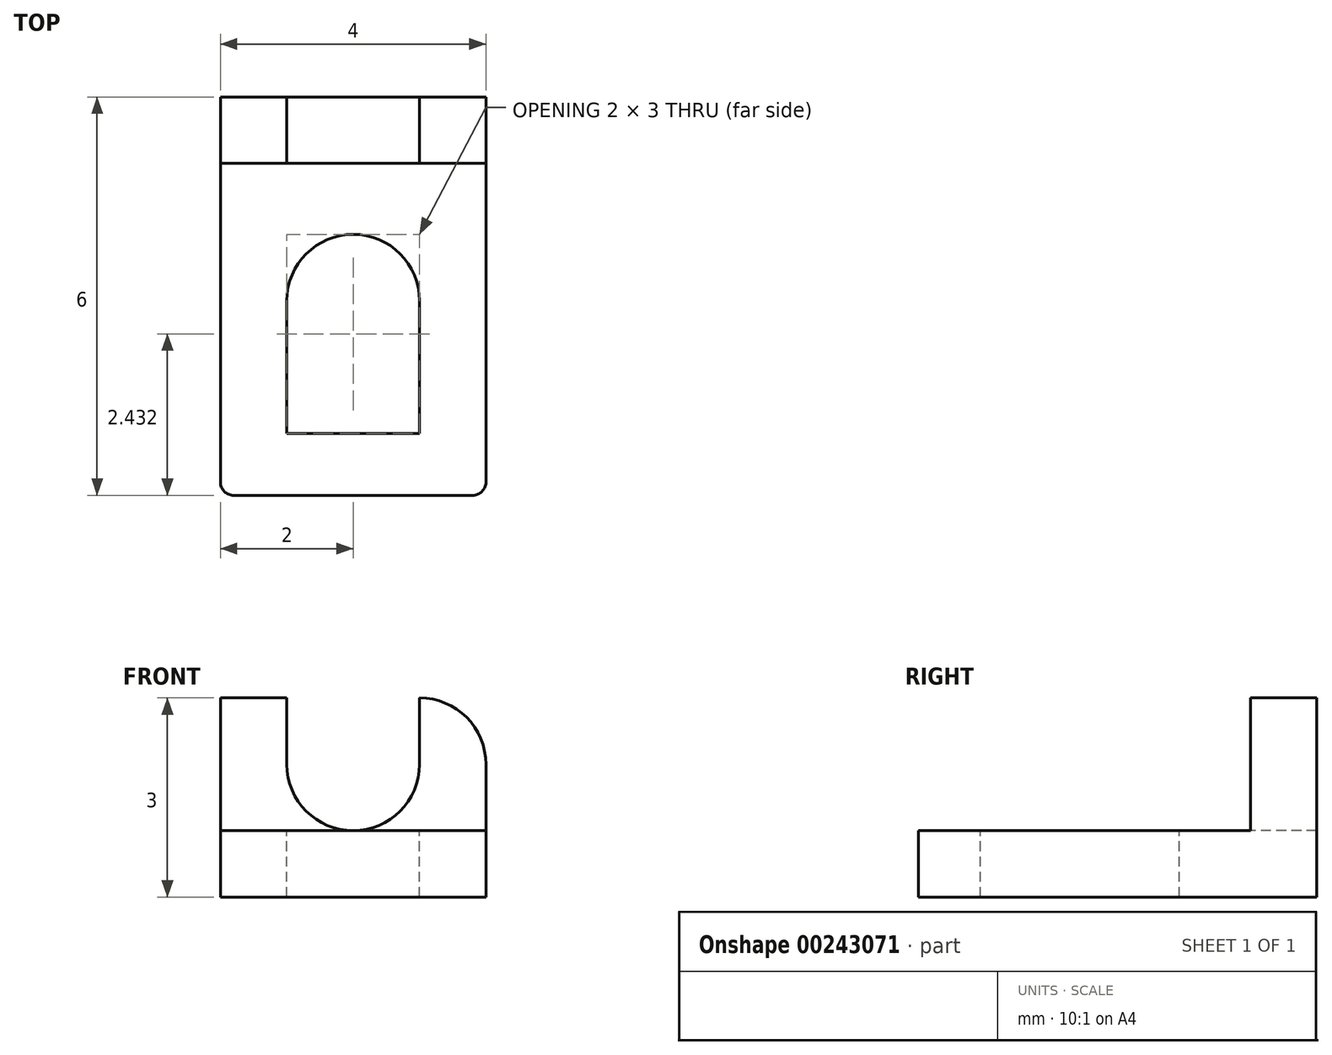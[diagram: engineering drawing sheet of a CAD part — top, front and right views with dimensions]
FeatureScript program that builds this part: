
annotation { "Feature Type Name" : "Feature", "Feature Type Description" : "" }
export const myFeature = defineFeature(function(context is Context, id is Id, definition is map)
    precondition{}
    {
        {
            var Q0;
            Q0=qCreatedBy(makeId("Top.planeOp"),FACE);
            var sketch = newSketch(context, id + "F0", { "sketchPlane" : qUnion([Q0])});
            skLineSegment(sketch, "E0.bottom", {"start": v(0, 0) * mm, "end": v(4, 0) * mm});
            skLineSegment(sketch, "E0.top", {"start": v(0, 5) * mm, "end": v(4, 5) * mm});
            skLineSegment(sketch, "E0.left", {"start": v(0, 0) * mm, "end": v(0, 5) * mm});
            skLineSegment(sketch, "E0.right", {"start": v(4, 0) * mm, "end": v(4, 5) * mm});
            skSolve(sketch);
        }
        {
            var Q0;
            Q0 = qSketchRegion(id + "F0", true);
            extrude(context, id + "F1", {"entities" : qUnion([Q0]), "depth" : 1 * mm});
        }
        {
            var Q0;
            Q0=makeQuery(id+"F1.opExtrude","SWEPT_EDGE",EDGE,{"disambiguationData":[OSD([sQuery(id+"F0.wireOp",EDGE,"E0.bottom"),sQuery(id+"F0.wireOp",EDGE,"E0.right")])]});
            fillet(context, id + "F2", {"entities" : qUnion([Q0]), "radius" : 0.2 * mm, "tangentPropagation" : true, "allowEdgeOverflow" : false});
        }
        {
            var Q0;
            Q0=makeQuery(id+"F1.opExtrude","SWEPT_EDGE",EDGE,{"disambiguationData":[OSD([sQuery(id+"F0.wireOp",EDGE,"E0.bottom"),sQuery(id+"F0.wireOp",EDGE,"E0.left")])]});
            fillet(context, id + "F3", {"entities" : qUnion([Q0]), "radius" : 0.2 * mm, "tangentPropagation" : true, "allowEdgeOverflow" : false});
        }
        {
            var Q0;
            Q0=makeQuery(id+"F1.opExtrude","CAP_FACE",FACE,{"disambiguationData":[OSD([sQuery(id+"F0.wireOp",EDGE,"E0.bottom"),sQuery(id+"F0.wireOp",EDGE,"E0.top"),sQuery(id+"F0.wireOp",EDGE,"E0.left"),sQuery(id+"F0.wireOp",EDGE,"E0.right")])],"isStart":false});
            var sketch = newSketch(context, id + "F4", { "sketchPlane" : qUnion([Q0])});
            skLineSegment(sketch, "E1", {"start": v(0, 0) * mm, "end": v(0, 0.93) * mm, "construction": true});
            skLineSegment(sketch, "E2", {"start": v(1, 0.93) * mm, "end": v(1, 2.93) * mm});
            skLineSegment(sketch, "E3", {"start": v(3, 2.93) * mm, "end": v(3, 0.93) * mm});
            skLineSegment(sketch, "E4", {"start": v(3, 0.93) * mm, "end": v(1, 0.93) * mm});
            skArc(sketch, "E5", {"start": v(3, 2.93) * mm, "mid": v(2, 3.93) * mm, "end": v(1, 2.93) * mm});
            skSolve(sketch);
        }
        {
            var Q0;
            Q0 = qSketchRegion(id + "F4", true);
            extrude(context, id + "F5", {"entities" : qUnion([Q0]), "operationType" : NewBodyOperationType.REMOVE, "oppositeDirection" : true, "depth" : 25 * mm});
        }
        {
            var Q0;
            Q0=makeQuery(id+"F1.opExtrude","SWEPT_FACE",FACE,{"disambiguationData":[OSD([sQuery(id+"F0.wireOp",EDGE,"E0.top")])]});
            var sketch = newSketch(context, id + "F6", { "sketchPlane" : qUnion([Q0])});
            skLineSegment(sketch, "E6", {"start": v(-4, 1) * mm, "end": v(-4, 3) * mm});
            skLineSegment(sketch, "E7", {"start": v(-4, 3) * mm, "end": v(-3, 3) * mm});
            skLineSegment(sketch, "E8", {"start": v(-3, 3) * mm, "end": v(-3, 2) * mm});
            skLineSegment(sketch, "E9", {"start": v(-1, 2) * mm, "end": v(-1, 3) * mm});
            skLineSegment(sketch, "E10", {"start": v(-1, 3) * mm, "end": v(0, 3) * mm});
            skLineSegment(sketch, "E11", {"start": v(0, 3) * mm, "end": v(0, 1) * mm});
            skArc(sketch, "E12", {"start": v(-3, 2) * mm, "mid": v(-2, 1) * mm, "end": v(-1, 2) * mm});
            skLineSegment(sketch, "E13", {"start": v(-4, 1) * mm, "end": v(-4, 0) * mm});
            skLineSegment(sketch, "E14", {"start": v(-4, 0) * mm, "end": v(0, 0) * mm});
            skLineSegment(sketch, "E15", {"start": v(0, 0) * mm, "end": v(0, 1) * mm});
            skSolve(sketch);
        }
        {
            var Q0;
            Q0 = qSketchRegion(id + "F6", true);
            extrude(context, id + "F7", {"entities" : qUnion([Q0]), "operationType" : NewBodyOperationType.ADD, "depth" : 1 * mm});
        }
        {
            var Q0;
            Q0=makeQuery(id+"F7.opExtrude","SWEPT_EDGE",EDGE,{"disambiguationData":[OSD([sQuery(id+"F6.wireOp",EDGE,"E6"),sQuery(id+"F6.wireOp",EDGE,"E7")])]});
            fillet(context, id + "F8", {"entities" : qUnion([Q0]), "radius" : 1 * mm, "tangentPropagation" : true, "allowEdgeOverflow" : false});
        }
    });
